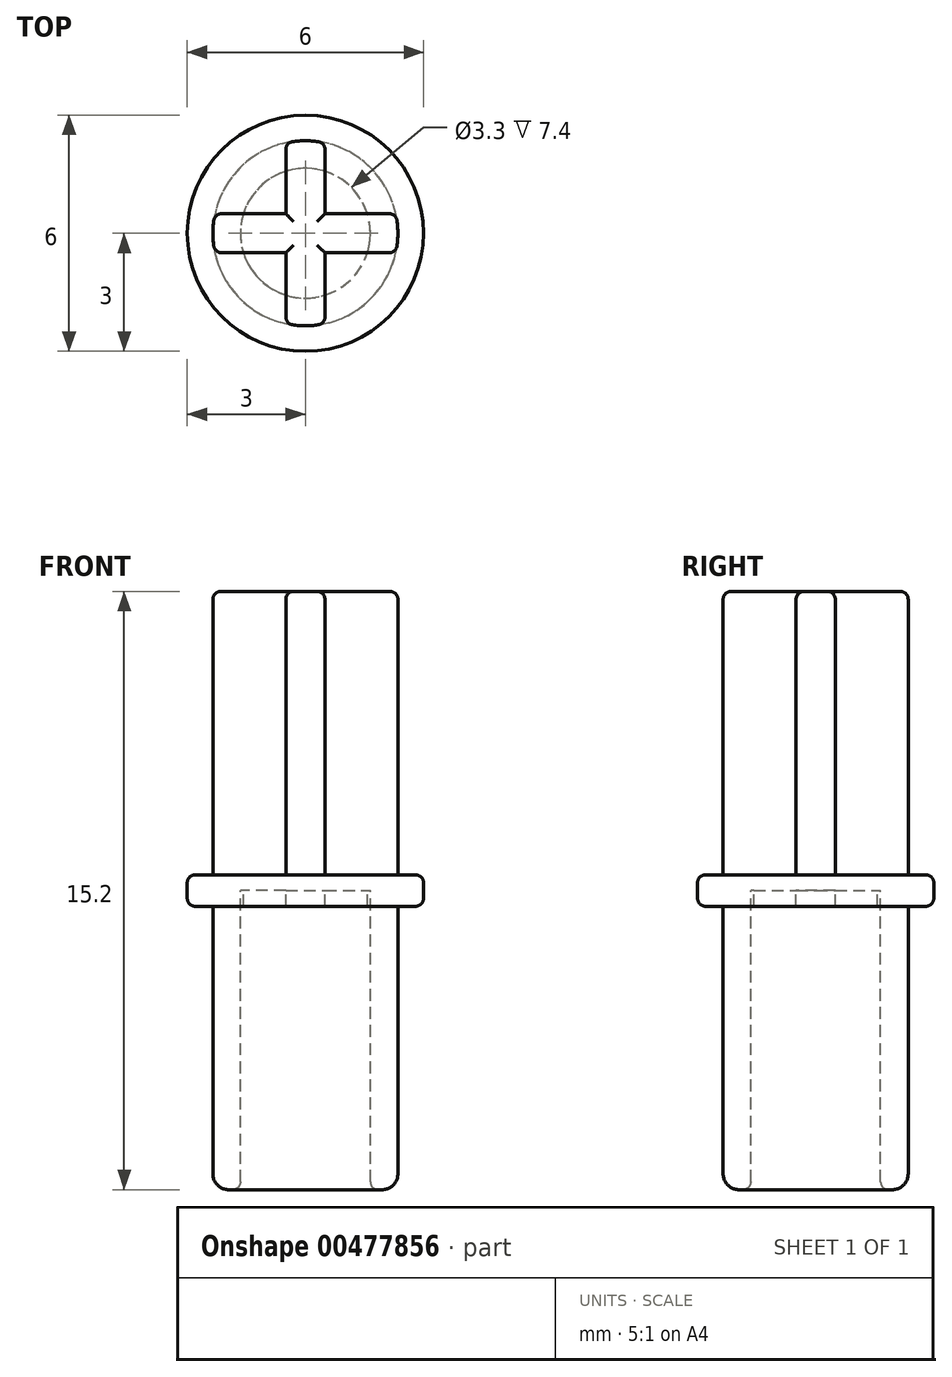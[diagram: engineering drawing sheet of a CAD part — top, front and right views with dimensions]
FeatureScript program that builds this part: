
annotation { "Feature Type Name" : "Feature", "Feature Type Description" : "" }
export const myFeature = defineFeature(function(context is Context, id is Id, definition is map)
    precondition{}
    {
        {
            var Q0;
            Q0=qCreatedBy(makeId("Top.planeOp"),FACE);
            var sketch = newSketch(context, id + "F0", { "sketchPlane" : qUnion([Q0])});
            skCircle(sketch, "E0", {"center": v(0, 0) * mm, "radius": 3 * mm});
            skCircle(sketch, "E1", {"center": v(0, 0) * mm, "radius": 2.35 * mm});
            skArc(sketch, "E2", {"start": v(-1.57, -0.5) * mm, "mid": v(-1.17, -1.17) * mm, "end": v(-0.5, -1.57) * mm});
            skLineSegment(sketch, "E3", {"start": v(-0.5, 0.5) * mm, "end": v(-2.3, 0.5) * mm});
            skLineSegment(sketch, "E4.MirrorCS", {"start": v(0.5, 0.5) * mm, "end": v(2.3, 0.5) * mm});
            skLineSegment(sketch, "E5.MirrorCS", {"start": v(-0.5, -0.5) * mm, "end": v(-2.3, -0.5) * mm});
            skLineSegment(sketch, "E6.MirrorCS", {"start": v(-0.5, -2.3) * mm, "end": v(-0.5, -0.5) * mm});
            skLineSegment(sketch, "E7.MirrorCS", {"start": v(0.5, -2.3) * mm, "end": v(0.5, -0.5) * mm});
            skLineSegment(sketch, "E8.MirrorCS", {"start": v(0.5, -0.5) * mm, "end": v(2.3, -0.5) * mm});
            skArc(sketch, "E9.trimOffspring", {"start": v(0.5, -1.57) * mm, "mid": v(1.17, -1.17) * mm, "end": v(1.57, -0.5) * mm});
            skArc(sketch, "E10.trimOffspring", {"start": v(1.57, 0.5) * mm, "mid": v(1.17, 1.17) * mm, "end": v(0.5, 1.57) * mm});
            skArc(sketch, "E11.trimOffspring", {"start": v(-0.5, 1.57) * mm, "mid": v(-1.17, 1.17) * mm, "end": v(-1.57, 0.5) * mm});
            skCircle(sketch, "E12", {"center": v(0, 0) * mm, "radius": 1.65 * mm});
            skLineSegment(sketch, "E13", {"start": v(-0.5, 0.5) * mm, "end": v(-0.5, 2.3) * mm});
            skLineSegment(sketch, "E14", {"start": v(0.5, 0.5) * mm, "end": v(0.5, 2.3) * mm});
            skSolve(sketch);
        }
        {
            var Q0;
            {var subQ10=sQuery(id+"F0.wireOp",EDGE,"E13");var subQ11=sQuery(id+"F0.wireOp",EDGE,"E3");var subQ12=makeQuery(id+"F0.imprint","INTERSECT",VERTEX,{"derivedFrom":[subQ11,subQ10]});Q0=makeQuery(id+"F0.imprint","IMPRINT",FACE,{"disambiguationData":[TD([[makeQuery(id+"F0.imprint","IMPRINT",EDGE,{"disambiguationData":[TD([[subQ12,-1.0]])],"derivedFrom":subQ11}),1.0]])]});}
            var Q1;
            {var subQ0=sQuery(id+"F0.wireOp",EDGE,"E3");var subQ1=sQuery(id+"F0.wireOp",EDGE,"E1");var subQ2=makeQuery(id+"F0.imprint","INTERSECT",VERTEX,{"derivedFrom":[subQ1,subQ0]});Q1=makeQuery(id+"F0.imprint","IMPRINT",FACE,{"disambiguationData":[TD([[makeQuery(id+"F0.imprint","IMPRINT",EDGE,{"disambiguationData":[TD([[subQ2,-1.0]])],"derivedFrom":subQ1}),1.0]])]});}
            var Q2;
            {var subQ0=sQuery(id+"F0.wireOp",EDGE,"E6.MirrorCS");var subQ1=sQuery(id+"F0.wireOp",EDGE,"E1");var subQ2=makeQuery(id+"F0.imprint","INTERSECT",VERTEX,{"derivedFrom":[subQ1,subQ0]});Q2=makeQuery(id+"F0.imprint","IMPRINT",FACE,{"disambiguationData":[TD([[makeQuery(id+"F0.imprint","IMPRINT",EDGE,{"disambiguationData":[TD([[subQ2,-1.0]])],"derivedFrom":subQ1}),1.0]])]});}
            var Q3;
            {var subQ0=sQuery(id+"F0.wireOp",EDGE,"E4.MirrorCS");var subQ1=sQuery(id+"F0.wireOp",EDGE,"E1");var subQ2=makeQuery(id+"F0.imprint","INTERSECT",VERTEX,{"derivedFrom":[subQ1,subQ0]});Q3=makeQuery(id+"F0.imprint","IMPRINT",FACE,{"disambiguationData":[TD([[makeQuery(id+"F0.imprint","IMPRINT",EDGE,{"disambiguationData":[TD([[subQ2,1.0]])],"derivedFrom":subQ1}),1.0]])]});}
            var Q4;
            {var subQ0=sQuery(id+"F0.wireOp",EDGE,"E13");var subQ1=sQuery(id+"F0.wireOp",EDGE,"E1");var subQ2=makeQuery(id+"F0.imprint","INTERSECT",VERTEX,{"derivedFrom":[subQ1,subQ0]});Q4=makeQuery(id+"F0.imprint","IMPRINT",FACE,{"disambiguationData":[TD([[makeQuery(id+"F0.imprint","IMPRINT",EDGE,{"disambiguationData":[TD([[subQ2,1.0]])],"derivedFrom":subQ1}),1.0]])]});}
            extrude(context, id + "F1", {"entities" : qUnion([Q0, Q1, Q2, Q3, Q4]), "depth" : 7.6 * mm, "offsetDistance" : 25 * mm});
        }
        {
            var Q0;
            {var subQ0=sQuery(id+"F0.wireOp",EDGE,"E3");var subQ1=sQuery(id+"F0.wireOp",EDGE,"E1");var subQ2=makeQuery(id+"F0.imprint","INTERSECT",VERTEX,{"derivedFrom":[subQ1,subQ0]});Q0=makeQuery(id+"F0.imprint","IMPRINT",FACE,{"disambiguationData":[TD([[makeQuery(id+"F0.imprint","IMPRINT",EDGE,{"disambiguationData":[TD([[subQ2,-1.0]])],"derivedFrom":subQ1}),1.0]])]});}
            var Q1;
            {var subQ0=sQuery(id+"F0.wireOp",EDGE,"E4.MirrorCS");var subQ1=sQuery(id+"F0.wireOp",EDGE,"E1");var subQ2=makeQuery(id+"F0.imprint","INTERSECT",VERTEX,{"derivedFrom":[subQ1,subQ0]});Q1=makeQuery(id+"F0.imprint","IMPRINT",FACE,{"disambiguationData":[TD([[makeQuery(id+"F0.imprint","IMPRINT",EDGE,{"disambiguationData":[TD([[subQ2,1.0]])],"derivedFrom":subQ1}),1.0]])]});}
            var Q2;
            {var subQ0=sQuery(id+"F0.wireOp",EDGE,"E6.MirrorCS");var subQ1=sQuery(id+"F0.wireOp",EDGE,"E1");var subQ2=makeQuery(id+"F0.imprint","INTERSECT",VERTEX,{"derivedFrom":[subQ1,subQ0]});Q2=makeQuery(id+"F0.imprint","IMPRINT",FACE,{"disambiguationData":[TD([[makeQuery(id+"F0.imprint","IMPRINT",EDGE,{"disambiguationData":[TD([[subQ2,-1.0]])],"derivedFrom":subQ1}),1.0]])]});}
            var Q3;
            {var subQ0=sQuery(id+"F0.wireOp",EDGE,"E13");var subQ1=sQuery(id+"F0.wireOp",EDGE,"E1");var subQ2=makeQuery(id+"F0.imprint","INTERSECT",VERTEX,{"derivedFrom":[subQ1,subQ0]});Q3=makeQuery(id+"F0.imprint","IMPRINT",FACE,{"disambiguationData":[TD([[makeQuery(id+"F0.imprint","IMPRINT",EDGE,{"disambiguationData":[TD([[subQ2,1.0]])],"derivedFrom":subQ1}),1.0]])]});}
            extrude(context, id + "F2", {"entities" : qUnion([Q0, Q1, Q2, Q3]), "operationType" : NewBodyOperationType.ADD, "oppositeDirection" : true, "depth" : 7.6 * mm, "offsetDistance" : 25 * mm});
        }
        {
            var Q0;
            {var subQ0=sQuery(id+"F0.wireOp",EDGE,"E7.MirrorCS");var subQ1=sQuery(id+"F0.wireOp",EDGE,"E1");var subQ2=makeQuery(id+"F0.imprint","INTERSECT",VERTEX,{"derivedFrom":[subQ1,subQ0]});Q0=makeQuery(id+"F0.imprint","IMPRINT",FACE,{"disambiguationData":[TD([[makeQuery(id+"F0.imprint","IMPRINT",EDGE,{"disambiguationData":[TD([[subQ2,-1.0]])],"derivedFrom":subQ1}),1.0]])]});}
            var Q1;
            {var subQ0=sQuery(id+"F0.wireOp",EDGE,"E4.MirrorCS");var subQ1=sQuery(id+"F0.wireOp",EDGE,"E1");var subQ2=makeQuery(id+"F0.imprint","INTERSECT",VERTEX,{"derivedFrom":[subQ1,subQ0]});Q1=makeQuery(id+"F0.imprint","IMPRINT",FACE,{"disambiguationData":[TD([[makeQuery(id+"F0.imprint","IMPRINT",EDGE,{"disambiguationData":[TD([[subQ2,-1.0]])],"derivedFrom":subQ1}),1.0]])]});}
            var Q2;
            {var subQ0=sQuery(id+"F0.wireOp",EDGE,"E3");var subQ1=sQuery(id+"F0.wireOp",EDGE,"E1");var subQ2=makeQuery(id+"F0.imprint","INTERSECT",VERTEX,{"derivedFrom":[subQ1,subQ0]});Q2=makeQuery(id+"F0.imprint","IMPRINT",FACE,{"disambiguationData":[TD([[makeQuery(id+"F0.imprint","IMPRINT",EDGE,{"disambiguationData":[TD([[subQ2,1.0]])],"derivedFrom":subQ1}),1.0]])]});}
            var Q3;
            {var subQ0=sQuery(id+"F0.wireOp",EDGE,"E5.MirrorCS");var subQ1=sQuery(id+"F0.wireOp",EDGE,"E1");var subQ2=makeQuery(id+"F0.imprint","INTERSECT",VERTEX,{"derivedFrom":[subQ1,subQ0]});Q3=makeQuery(id+"F0.imprint","IMPRINT",FACE,{"disambiguationData":[TD([[makeQuery(id+"F0.imprint","IMPRINT",EDGE,{"disambiguationData":[TD([[subQ2,-1.0]])],"derivedFrom":subQ1}),1.0]])]});}
            extrude(context, id + "F3", {"entities" : qUnion([Q0, Q1, Q2, Q3]), "operationType" : NewBodyOperationType.ADD, "oppositeDirection" : true, "depth" : 7.6 * mm, "offsetDistance" : 25 * mm});
        }
        {
            var Q0;
            Q0=makeQuery(id+"F0.imprint","IMPRINT",FACE,{"disambiguationData":[TD([[makeQuery(id+"F0.imprint","IMPRINT",EDGE,{"derivedFrom":sQuery(id+"F0.wireOp",EDGE,"E0")}),1.0]])]});
            var Q1;
            {var subQ0=sQuery(id+"F0.wireOp",EDGE,"E6.MirrorCS");var subQ1=sQuery(id+"F0.wireOp",EDGE,"E5.MirrorCS");var subQ2=makeQuery(id+"F0.imprint","INTERSECT",VERTEX,{"derivedFrom":[subQ1,subQ0]});Q1=makeQuery(id+"F0.imprint","IMPRINT",FACE,{"disambiguationData":[TD([[makeQuery(id+"F0.imprint","IMPRINT",EDGE,{"disambiguationData":[TD([[subQ2,-1.0]])],"derivedFrom":subQ1}),1.0]])]});}
            var Q2;
            {var subQ0=sQuery(id+"F0.wireOp",EDGE,"E5.MirrorCS");var subQ1=sQuery(id+"F0.wireOp",EDGE,"E1");var subQ2=makeQuery(id+"F0.imprint","INTERSECT",VERTEX,{"derivedFrom":[subQ1,subQ0]});Q2=makeQuery(id+"F0.imprint","IMPRINT",FACE,{"disambiguationData":[TD([[makeQuery(id+"F0.imprint","IMPRINT",EDGE,{"disambiguationData":[TD([[subQ2,-1.0]])],"derivedFrom":subQ1}),1.0]])]});}
            var Q3;
            {var subQ0=sQuery(id+"F0.wireOp",EDGE,"E8.MirrorCS");var subQ1=sQuery(id+"F0.wireOp",EDGE,"E7.MirrorCS");var subQ2=makeQuery(id+"F0.imprint","INTERSECT",VERTEX,{"derivedFrom":[subQ1,subQ0]});Q3=makeQuery(id+"F0.imprint","IMPRINT",FACE,{"disambiguationData":[TD([[makeQuery(id+"F0.imprint","IMPRINT",EDGE,{"disambiguationData":[TD([[subQ2,1.0]])],"derivedFrom":subQ1}),-1.0]])]});}
            var Q4;
            {var subQ0=sQuery(id+"F0.wireOp",EDGE,"E7.MirrorCS");var subQ1=sQuery(id+"F0.wireOp",EDGE,"E1");var subQ2=makeQuery(id+"F0.imprint","INTERSECT",VERTEX,{"derivedFrom":[subQ1,subQ0]});Q4=makeQuery(id+"F0.imprint","IMPRINT",FACE,{"disambiguationData":[TD([[makeQuery(id+"F0.imprint","IMPRINT",EDGE,{"disambiguationData":[TD([[subQ2,-1.0]])],"derivedFrom":subQ1}),1.0]])]});}
            var Q5;
            {var subQ0=sQuery(id+"F0.wireOp",EDGE,"E14");var subQ1=sQuery(id+"F0.wireOp",EDGE,"E4.MirrorCS");var subQ2=makeQuery(id+"F0.imprint","INTERSECT",VERTEX,{"derivedFrom":[subQ1,subQ0]});Q5=makeQuery(id+"F0.imprint","IMPRINT",FACE,{"disambiguationData":[TD([[makeQuery(id+"F0.imprint","IMPRINT",EDGE,{"disambiguationData":[TD([[subQ2,-1.0]])],"derivedFrom":subQ1}),1.0]])]});}
            var Q6;
            {var subQ0=sQuery(id+"F0.wireOp",EDGE,"E4.MirrorCS");var subQ1=sQuery(id+"F0.wireOp",EDGE,"E1");var subQ2=makeQuery(id+"F0.imprint","INTERSECT",VERTEX,{"derivedFrom":[subQ1,subQ0]});Q6=makeQuery(id+"F0.imprint","IMPRINT",FACE,{"disambiguationData":[TD([[makeQuery(id+"F0.imprint","IMPRINT",EDGE,{"disambiguationData":[TD([[subQ2,-1.0]])],"derivedFrom":subQ1}),1.0]])]});}
            var Q7;
            {var subQ0=sQuery(id+"F0.wireOp",EDGE,"E13");var subQ1=sQuery(id+"F0.wireOp",EDGE,"E3");var subQ2=makeQuery(id+"F0.imprint","INTERSECT",VERTEX,{"derivedFrom":[subQ1,subQ0]});Q7=makeQuery(id+"F0.imprint","IMPRINT",FACE,{"disambiguationData":[TD([[makeQuery(id+"F0.imprint","IMPRINT",EDGE,{"disambiguationData":[TD([[subQ2,-1.0]])],"derivedFrom":subQ1}),-1.0]])]});}
            var Q8;
            {var subQ0=sQuery(id+"F0.wireOp",EDGE,"E3");var subQ1=sQuery(id+"F0.wireOp",EDGE,"E1");var subQ2=makeQuery(id+"F0.imprint","INTERSECT",VERTEX,{"derivedFrom":[subQ1,subQ0]});Q8=makeQuery(id+"F0.imprint","IMPRINT",FACE,{"disambiguationData":[TD([[makeQuery(id+"F0.imprint","IMPRINT",EDGE,{"disambiguationData":[TD([[subQ2,1.0]])],"derivedFrom":subQ1}),1.0]])]});}
            extrude(context, id + "F4", {"entities" : qUnion([Q0, Q1, Q2, Q3, Q4, Q5, Q6, Q7, Q8]), "operationType" : NewBodyOperationType.ADD, "endBound" : BoundingType.SYMMETRIC, "depth" : 0.8 * mm, "offsetDistance" : 25 * mm});
        }
        {
            var Q0;
            {var subQ0=sQuery(id+"F0.wireOp",EDGE,"E6.MirrorCS");var subQ1=sQuery(id+"F0.wireOp",EDGE,"E1");Q0=makeQuery(id+"F2.boolean.opBoolean","MERGE",EDGE,{"derivedFrom":[makeQuery(id+"F1.opExtrude","SWEPT_EDGE",EDGE,{"disambiguationData":[OSD([subQ1,subQ0])]}),makeQuery(id+"F2.opExtrude","SWEPT_EDGE",EDGE,{"disambiguationData":[OSD([subQ1,subQ0])]})]});}
            var Q1;
            {var subQ0=sQuery(id+"F0.wireOp",EDGE,"E7.MirrorCS");var subQ1=sQuery(id+"F0.wireOp",EDGE,"E1");Q1=makeQuery(id+"F2.boolean.opBoolean","MERGE",EDGE,{"derivedFrom":[makeQuery(id+"F1.opExtrude","SWEPT_EDGE",EDGE,{"disambiguationData":[OSD([subQ1,subQ0])]}),makeQuery(id+"F2.opExtrude","SWEPT_EDGE",EDGE,{"disambiguationData":[OSD([subQ1,subQ0])]})]});}
            var Q2;
            {var subQ0=sQuery(id+"F0.wireOp",EDGE,"E5.MirrorCS");var subQ1=sQuery(id+"F0.wireOp",EDGE,"E1");Q2=makeQuery(id+"F2.boolean.opBoolean","MERGE",EDGE,{"derivedFrom":[makeQuery(id+"F1.opExtrude","SWEPT_EDGE",EDGE,{"disambiguationData":[OSD([subQ1,subQ0])]}),makeQuery(id+"F2.opExtrude","SWEPT_EDGE",EDGE,{"disambiguationData":[OSD([subQ1,subQ0])]})]});}
            var Q3;
            {var subQ0=sQuery(id+"F0.wireOp",EDGE,"E3");var subQ1=sQuery(id+"F0.wireOp",EDGE,"E1");Q3=makeQuery(id+"F2.boolean.opBoolean","MERGE",EDGE,{"derivedFrom":[makeQuery(id+"F1.opExtrude","SWEPT_EDGE",EDGE,{"disambiguationData":[OSD([subQ1,subQ0])]}),makeQuery(id+"F2.opExtrude","SWEPT_EDGE",EDGE,{"disambiguationData":[OSD([subQ1,subQ0])]})]});}
            var Q4;
            {var subQ0=sQuery(id+"F0.wireOp",EDGE,"E13");var subQ1=sQuery(id+"F0.wireOp",EDGE,"E1");Q4=makeQuery(id+"F2.boolean.opBoolean","MERGE",EDGE,{"derivedFrom":[makeQuery(id+"F1.opExtrude","SWEPT_EDGE",EDGE,{"disambiguationData":[OSD([subQ1,subQ0])]}),makeQuery(id+"F2.opExtrude","SWEPT_EDGE",EDGE,{"disambiguationData":[OSD([subQ1,subQ0])]})]});}
            var Q5;
            {var subQ0=sQuery(id+"F0.wireOp",EDGE,"E8.MirrorCS");var subQ1=sQuery(id+"F0.wireOp",EDGE,"E1");Q5=makeQuery(id+"F2.boolean.opBoolean","MERGE",EDGE,{"derivedFrom":[makeQuery(id+"F1.opExtrude","SWEPT_EDGE",EDGE,{"disambiguationData":[OSD([subQ1,subQ0])]}),makeQuery(id+"F2.opExtrude","SWEPT_EDGE",EDGE,{"disambiguationData":[OSD([subQ1,subQ0])]})]});}
            var Q6;
            {var subQ0=sQuery(id+"F0.wireOp",EDGE,"E4.MirrorCS");var subQ1=sQuery(id+"F0.wireOp",EDGE,"E1");Q6=makeQuery(id+"F2.boolean.opBoolean","MERGE",EDGE,{"derivedFrom":[makeQuery(id+"F1.opExtrude","SWEPT_EDGE",EDGE,{"disambiguationData":[OSD([subQ1,subQ0])]}),makeQuery(id+"F2.opExtrude","SWEPT_EDGE",EDGE,{"disambiguationData":[OSD([subQ1,subQ0])]})]});}
            var Q7;
            {var subQ0=sQuery(id+"F0.wireOp",EDGE,"E14");var subQ1=sQuery(id+"F0.wireOp",EDGE,"E1");Q7=makeQuery(id+"F2.boolean.opBoolean","MERGE",EDGE,{"derivedFrom":[makeQuery(id+"F1.opExtrude","SWEPT_EDGE",EDGE,{"disambiguationData":[OSD([subQ1,subQ0])]}),makeQuery(id+"F2.opExtrude","SWEPT_EDGE",EDGE,{"disambiguationData":[OSD([subQ1,subQ0])]})]});}
            var Q8;
            Q8=makeQuery(id+"F4.opExtrude","CAP_EDGE",EDGE,{"disambiguationData":[OSD([sQuery(id+"F0.wireOp",EDGE,"E0")])],"isStart":false});
            var Q9;
            Q9=makeQuery(id+"F4.opExtrude","CAP_EDGE",EDGE,{"disambiguationData":[OSD([sQuery(id+"F0.wireOp",EDGE,"E0")])],"isStart":true});
            var Q10;
            {var subQ0=sQuery(id+"F0.wireOp",EDGE,"E12");var subQ1=makeQuery(id+"F0.imprint","INTERSECT",VERTEX,{"derivedFrom":[sQuery(id+"F0.wireOp",EDGE,"E7.MirrorCS"),subQ0]});var subQ3=makeQuery(id+"F0.imprint","INTERSECT",VERTEX,{"derivedFrom":[sQuery(id+"F0.wireOp",EDGE,"E5.MirrorCS"),subQ0]});var subQ4=makeQuery(id+"F0.imprint","INTERSECT",VERTEX,{"derivedFrom":[sQuery(id+"F0.wireOp",EDGE,"E6.MirrorCS"),subQ0]});var subQ5=makeQuery(id+"F0.imprint","INTERSECT",VERTEX,{"derivedFrom":[sQuery(id+"F0.wireOp",EDGE,"E3"),subQ0]});var subQ7=makeQuery(id+"F0.imprint","INTERSECT",VERTEX,{"derivedFrom":[sQuery(id+"F0.wireOp",EDGE,"E4.MirrorCS"),subQ0]});var subQ8=makeQuery(id+"F0.imprint","INTERSECT",VERTEX,{"derivedFrom":[subQ0,sQuery(id+"F0.wireOp",EDGE,"E14")]});Q10=makeQuery(id+"F3.boolean.opBoolean","MERGE",EDGE,{"derivedFrom":[makeQuery(id+"F2.opExtrude","CAP_EDGE",EDGE,{"disambiguationData":[OSD([subQ0]),TDD([makeQuery(id+"F0.imprint","IMPRINT",EDGE,{"disambiguationData":[TD([[subQ8,-1.0]])],"derivedFrom":subQ0})])],"isStart":false}),makeQuery(id+"F2.opExtrude","CAP_EDGE",EDGE,{"disambiguationData":[OSD([subQ0]),TDD([makeQuery(id+"F0.imprint","IMPRINT",EDGE,{"disambiguationData":[TD([[subQ5,-1.0]])],"derivedFrom":subQ0})])],"isStart":false}),makeQuery(id+"F2.opExtrude","CAP_EDGE",EDGE,{"disambiguationData":[OSD([subQ0]),TDD([makeQuery(id+"F0.imprint","IMPRINT",EDGE,{"disambiguationData":[TD([[subQ4,-1.0]])],"derivedFrom":subQ0})])],"isStart":false}),makeQuery(id+"F2.opExtrude","CAP_EDGE",EDGE,{"disambiguationData":[OSD([subQ0]),TDD([makeQuery(id+"F0.imprint","IMPRINT",EDGE,{"disambiguationData":[TD([[subQ7,1.0]])],"derivedFrom":subQ0})])],"isStart":false}),makeQuery(id+"F3.opExtrude","CAP_EDGE",EDGE,{"disambiguationData":[OSD([subQ0]),TDD([makeQuery(id+"F0.imprint","IMPRINT",EDGE,{"disambiguationData":[TD([[subQ7,-1.0]])],"derivedFrom":subQ0})])],"isStart":false}),makeQuery(id+"F3.opExtrude","CAP_EDGE",EDGE,{"disambiguationData":[OSD([subQ0]),TDD([makeQuery(id+"F0.imprint","IMPRINT",EDGE,{"disambiguationData":[TD([[subQ5,1.0]])],"derivedFrom":subQ0})])],"isStart":false}),makeQuery(id+"F3.opExtrude","CAP_EDGE",EDGE,{"disambiguationData":[OSD([subQ0]),TDD([makeQuery(id+"F0.imprint","IMPRINT",EDGE,{"disambiguationData":[TD([[subQ3,-1.0]])],"derivedFrom":subQ0})])],"isStart":false}),makeQuery(id+"F3.opExtrude","CAP_EDGE",EDGE,{"disambiguationData":[OSD([subQ0]),TDD([makeQuery(id+"F0.imprint","IMPRINT",EDGE,{"disambiguationData":[TD([[subQ1,-1.0]])],"derivedFrom":subQ0})])],"isStart":false})]});}
            fillet(context, id + "F5", {"entities" : qUnion([Q0, Q1, Q2, Q3, Q4, Q5, Q6, Q7, Q8, Q9, Q10]), "radius" : 0.2 * mm, "tangentPropagation" : true, "allowEdgeOverflow" : false});
        }
        {
            var Q0;
            {var subQ0=sQuery(id+"F0.wireOp",EDGE,"E1");var subQ1=makeQuery(id+"F0.imprint","INTERSECT",VERTEX,{"derivedFrom":[subQ0,sQuery(id+"F0.wireOp",EDGE,"E7.MirrorCS")]});var subQ3=makeQuery(id+"F0.imprint","INTERSECT",VERTEX,{"derivedFrom":[subQ0,sQuery(id+"F0.wireOp",EDGE,"E5.MirrorCS")]});var subQ4=makeQuery(id+"F0.imprint","INTERSECT",VERTEX,{"derivedFrom":[subQ0,sQuery(id+"F0.wireOp",EDGE,"E6.MirrorCS")]});var subQ5=makeQuery(id+"F0.imprint","INTERSECT",VERTEX,{"derivedFrom":[subQ0,sQuery(id+"F0.wireOp",EDGE,"E3")]});var subQ6=makeQuery(id+"F0.imprint","INTERSECT",VERTEX,{"derivedFrom":[subQ0,sQuery(id+"F0.wireOp",EDGE,"E13")]});var subQ7=makeQuery(id+"F0.imprint","INTERSECT",VERTEX,{"derivedFrom":[subQ0,sQuery(id+"F0.wireOp",EDGE,"E4.MirrorCS")]});Q0=makeQuery(id+"F3.boolean.opBoolean","MERGE",EDGE,{"derivedFrom":[makeQuery(id+"F2.opExtrude","CAP_EDGE",EDGE,{"disambiguationData":[OSD([subQ0]),TDD([makeQuery(id+"F0.imprint","IMPRINT",EDGE,{"disambiguationData":[TD([[subQ6,1.0]])],"derivedFrom":subQ0})])],"isStart":false}),makeQuery(id+"F2.opExtrude","CAP_EDGE",EDGE,{"disambiguationData":[OSD([subQ0]),TDD([makeQuery(id+"F0.imprint","IMPRINT",EDGE,{"disambiguationData":[TD([[subQ5,-1.0]])],"derivedFrom":subQ0})])],"isStart":false}),makeQuery(id+"F2.opExtrude","CAP_EDGE",EDGE,{"disambiguationData":[OSD([subQ0]),TDD([makeQuery(id+"F0.imprint","IMPRINT",EDGE,{"disambiguationData":[TD([[subQ4,-1.0]])],"derivedFrom":subQ0})])],"isStart":false}),makeQuery(id+"F2.opExtrude","CAP_EDGE",EDGE,{"disambiguationData":[OSD([subQ0]),TDD([makeQuery(id+"F0.imprint","IMPRINT",EDGE,{"disambiguationData":[TD([[subQ7,1.0]])],"derivedFrom":subQ0})])],"isStart":false}),makeQuery(id+"F3.opExtrude","CAP_EDGE",EDGE,{"disambiguationData":[OSD([subQ0]),TDD([makeQuery(id+"F0.imprint","IMPRINT",EDGE,{"disambiguationData":[TD([[subQ7,-1.0]])],"derivedFrom":subQ0})])],"isStart":false}),makeQuery(id+"F3.opExtrude","CAP_EDGE",EDGE,{"disambiguationData":[OSD([subQ0]),TDD([makeQuery(id+"F0.imprint","IMPRINT",EDGE,{"disambiguationData":[TD([[subQ5,1.0]])],"derivedFrom":subQ0})])],"isStart":false}),makeQuery(id+"F3.opExtrude","CAP_EDGE",EDGE,{"disambiguationData":[OSD([subQ0]),TDD([makeQuery(id+"F0.imprint","IMPRINT",EDGE,{"disambiguationData":[TD([[subQ3,-1.0]])],"derivedFrom":subQ0})])],"isStart":false}),makeQuery(id+"F3.opExtrude","CAP_EDGE",EDGE,{"disambiguationData":[OSD([subQ0]),TDD([makeQuery(id+"F0.imprint","IMPRINT",EDGE,{"disambiguationData":[TD([[subQ1,-1.0]])],"derivedFrom":subQ0})])],"isStart":false})]});}
            fillet(context, id + "F6", {"entities" : qUnion([Q0]), "radius" : 0.4 * mm, "tangentPropagation" : true, "allowEdgeOverflow" : false});
        }
        {
            var Q0;
            Q0=makeQuery(id+"F1.opExtrude","CAP_FACE",FACE,{"disambiguationData":[OSD([sQuery(id+"F0.wireOp",EDGE,"E1"),sQuery(id+"F0.wireOp",EDGE,"E3"),sQuery(id+"F0.wireOp",EDGE,"E4.MirrorCS"),sQuery(id+"F0.wireOp",EDGE,"E5.MirrorCS"),sQuery(id+"F0.wireOp",EDGE,"E6.MirrorCS"),sQuery(id+"F0.wireOp",EDGE,"E7.MirrorCS"),sQuery(id+"F0.wireOp",EDGE,"E8.MirrorCS"),sQuery(id+"F0.wireOp",EDGE,"E13"),sQuery(id+"F0.wireOp",EDGE,"E14")])],"isStart":false});
            fillet(context, id + "F7", {"entities" : qUnion([Q0]), "radius" : 0.2 * mm, "tangentPropagation" : true, "allowEdgeOverflow" : false});
        }
    });
